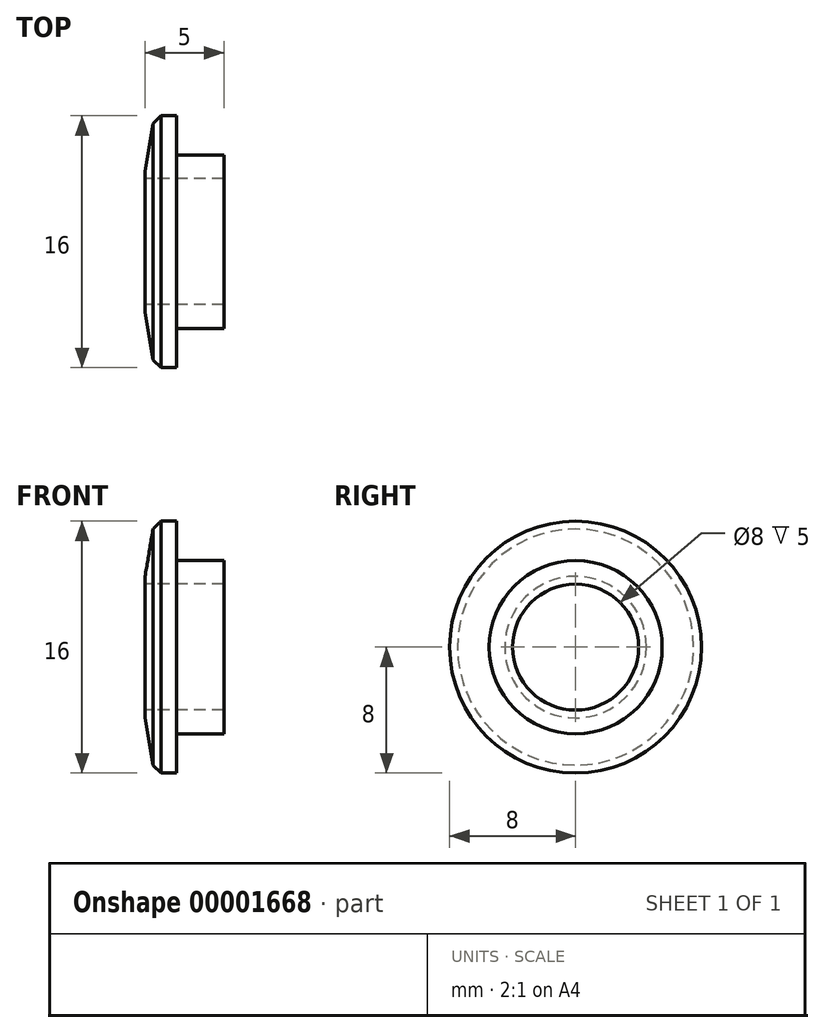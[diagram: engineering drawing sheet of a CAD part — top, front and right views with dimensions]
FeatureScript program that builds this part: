
annotation { "Feature Type Name" : "Feature", "Feature Type Description" : "" }
export const myFeature = defineFeature(function(context is Context, id is Id, definition is map)
    precondition{}
    {
        {
            var Q0;
            Q0=qCreatedBy(makeId("Front.planeOp"),FACE);
            var sketch = newSketch(context, id + "F0", { "sketchPlane" : qUnion([Q0])});
            skLineSegment(sketch, "E0", {"start": v(-5, 4) * mm, "end": v(-5, 0) * mm, "construction": true});
            skLineSegment(sketch, "E1", {"start": v(-5, 0) * mm, "end": v(0, 0) * mm, "construction": true});
            skLineSegment(sketch, "E2", {"start": v(0, 0) * mm, "end": v(0, 4) * mm, "construction": true});
            skLineSegment(sketch, "E3", {"start": v(0, 4) * mm, "end": v(-5, 4) * mm});
            skLineSegment(sketch, "E4", {"start": v(-5, 4) * mm, "end": v(-5, 4.5) * mm});
            skLineSegment(sketch, "E5", {"start": v(-5, 4.5) * mm, "end": v(-4.5, 7.5) * mm});
            skLineSegment(sketch, "E6", {"start": v(-4.5, 7.5) * mm, "end": v(-4, 8) * mm});
            skLineSegment(sketch, "E7", {"start": v(-4, 8) * mm, "end": v(-3, 8) * mm});
            skLineSegment(sketch, "E8", {"start": v(-3, 8) * mm, "end": v(-3, 5.5) * mm});
            skLineSegment(sketch, "E9", {"start": v(-3, 5.5) * mm, "end": v(0, 5.5) * mm});
            skLineSegment(sketch, "E10", {"start": v(0, 5.5) * mm, "end": v(0, 4) * mm});
            skSolve(sketch);
        }
        {
            var Q0;
            Q0=makeQuery(id+"F0.imprint","IMPRINT",FACE,{"disambiguationData":[TD([[makeQuery(id+"F0.imprint","IMPRINT",EDGE,{"derivedFrom":sQuery(id+"F0.wireOp",EDGE,"E3")}),-1.0]])]});
            var Q1;
            Q1=sQuery(id+"F0.wireOp",EDGE,"E1");
            revolve(context, id + "F1", {"entities" : qUnion([Q0]), "axis" : qUnion([Q1]), "revolveType" : RevolveType.FULL});
        }
    });
